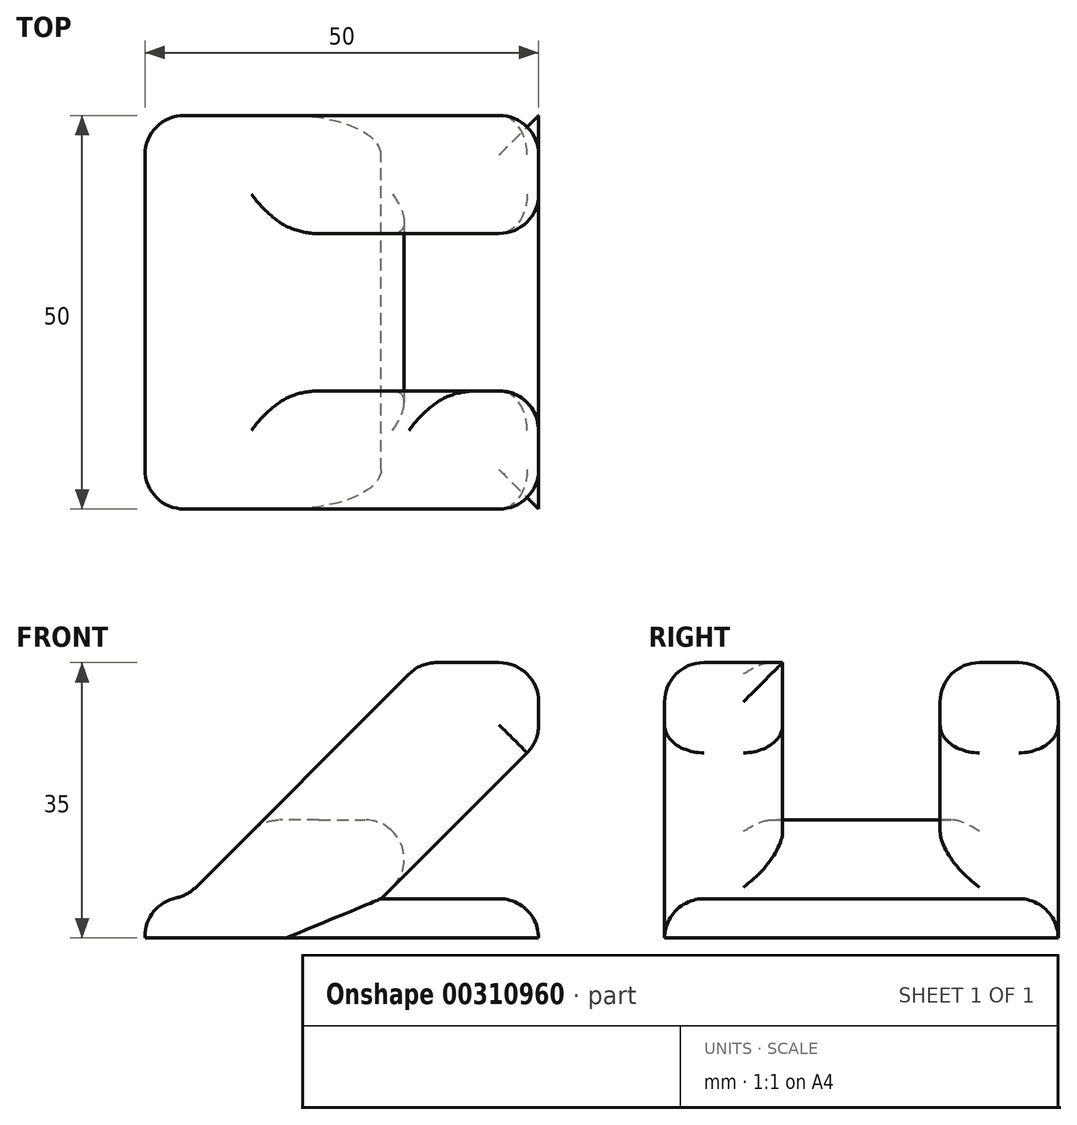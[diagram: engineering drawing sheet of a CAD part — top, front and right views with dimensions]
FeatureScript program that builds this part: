
annotation { "Feature Type Name" : "Feature", "Feature Type Description" : "" }
export const myFeature = defineFeature(function(context is Context, id is Id, definition is map)
    precondition{}
    {
        {
            var Q0;
            Q0=qCreatedBy(makeId("Front.planeOp"),FACE);
            var sketch = newSketch(context, id + "F0", { "sketchPlane" : qUnion([Q0])});
            skLineSegment(sketch, "E0", {"start": v(0, 0) * mm, "end": v(0, 5) * mm});
            skLineSegment(sketch, "E1", {"start": v(0, 5) * mm, "end": v(5, 5) * mm});
            skLineSegment(sketch, "E2", {"start": v(5, 5) * mm, "end": v(35, 35) * mm});
            skLineSegment(sketch, "E3", {"start": v(35, 35) * mm, "end": v(50, 35) * mm});
            skLineSegment(sketch, "E4", {"start": v(50, 35) * mm, "end": v(50, 25) * mm});
            skLineSegment(sketch, "E5", {"start": v(50, 25) * mm, "end": v(30, 5) * mm});
            skLineSegment(sketch, "E6", {"start": v(30, 5) * mm, "end": v(50, 5) * mm});
            skLineSegment(sketch, "E7", {"start": v(50, 5) * mm, "end": v(50, 0) * mm});
            skLineSegment(sketch, "E8", {"start": v(50, 0) * mm, "end": v(0, 0) * mm});
            skSolve(sketch);
        }
        {
            var Q0;
            Q0 = qSketchRegion(id + "F0", true);
            extrude(context, id + "F1", {"entities" : qUnion([Q0]), "depth" : 50 * mm});
        }
        {
            var Q0;
            Q0=makeQuery(id+"F1.opExtrude","SWEPT_FACE",FACE,{"disambiguationData":[OSD([sQuery(id+"F0.wireOp",EDGE,"E4")])]});
            var sketch = newSketch(context, id + "F2", { "sketchPlane" : qUnion([Q0])});
            skLineSegment(sketch, "E9.bottom", {"start": v(-35, 35) * mm, "end": v(-15, 35) * mm});
            skLineSegment(sketch, "E9.top", {"start": v(-35, 15) * mm, "end": v(-15, 15) * mm});
            skLineSegment(sketch, "E9.left", {"start": v(-35, 35) * mm, "end": v(-35, 15) * mm});
            skLineSegment(sketch, "E9.right", {"start": v(-15, 35) * mm, "end": v(-15, 15) * mm});
            skSolve(sketch);
        }
        {
            var Q0;
            Q0 = qSketchRegion(id + "F2", true);
            extrude(context, id + "F3", {"entities" : qUnion([Q0]), "operationType" : NewBodyOperationType.REMOVE, "endBound" : BoundingType.THROUGH_ALL, "oppositeDirection" : true, "depth" : 25 * mm});
        }
        {
            var Q0;
            Q0=makeQuery(id+"F1.opExtrude","CAP_EDGE",EDGE,{"disambiguationData":[OSD([sQuery(id+"F0.wireOp",EDGE,"E5")])],"isStart":false});
            var Q1;
            Q1=makeQuery(id+"F1.opExtrude","CAP_EDGE",EDGE,{"disambiguationData":[OSD([sQuery(id+"F0.wireOp",EDGE,"E4")])],"isStart":false});
            var Q2;
            Q2=makeQuery(id+"F3.boolean.opBoolean","COPY",EDGE,{"derivedFrom":makeQuery(id+"F3.opExtrude","CAP_EDGE",EDGE,{"disambiguationData":[OSD([sQuery(id+"F2.wireOp",EDGE,"E9.left")])],"isStart":true})});
            var Q3;
            Q3=makeQuery(id+"F3.boolean.opBoolean","INTERSECT",EDGE,{"derivedFrom":[makeQuery(id+"F1.opExtrude","SWEPT_FACE",FACE,{"disambiguationData":[OSD([sQuery(id+"F0.wireOp",EDGE,"E5")])]}),makeQuery(id+"F3.opExtrude","SWEPT_FACE",FACE,{"disambiguationData":[OSD([sQuery(id+"F2.wireOp",EDGE,"E9.left")])]})]});
            var Q4;
            Q4=makeQuery(id+"F3.boolean.opBoolean","INTERSECT",EDGE,{"derivedFrom":[makeQuery(id+"F1.opExtrude","SWEPT_FACE",FACE,{"disambiguationData":[OSD([sQuery(id+"F0.wireOp",EDGE,"E5")])]}),makeQuery(id+"F3.opExtrude","SWEPT_FACE",FACE,{"disambiguationData":[OSD([sQuery(id+"F2.wireOp",EDGE,"E9.top")])]})]});
            var Q5;
            Q5=makeQuery(id+"F3.boolean.opBoolean","INTERSECT",EDGE,{"derivedFrom":[makeQuery(id+"F1.opExtrude","SWEPT_FACE",FACE,{"disambiguationData":[OSD([sQuery(id+"F0.wireOp",EDGE,"E5")])]}),makeQuery(id+"F3.opExtrude","SWEPT_FACE",FACE,{"disambiguationData":[OSD([sQuery(id+"F2.wireOp",EDGE,"E9.right")])]})]});
            var Q6;
            Q6=makeQuery(id+"F3.boolean.opBoolean","COPY",EDGE,{"derivedFrom":makeQuery(id+"F3.opExtrude","CAP_EDGE",EDGE,{"disambiguationData":[OSD([sQuery(id+"F2.wireOp",EDGE,"E9.right")])],"isStart":true})});
            var Q7;
            Q7=makeQuery(id+"F1.opExtrude","CAP_EDGE",EDGE,{"disambiguationData":[OSD([sQuery(id+"F0.wireOp",EDGE,"E4")])],"isStart":true});
            var Q8;
            Q8=makeQuery(id+"F1.opExtrude","CAP_EDGE",EDGE,{"disambiguationData":[OSD([sQuery(id+"F0.wireOp",EDGE,"E5")])],"isStart":true});
            var Q9;
            {var subQ0=sQuery(id+"F0.wireOp",EDGE,"E3");var subQ1=sQuery(id+"F0.wireOp",EDGE,"E2");Q9=makeQuery(id+"F3.boolean.opBoolean","SPLIT",EDGE,{"disambiguationData":[TD([makeQuery(id+"F3.opExtrude","SWEPT_FACE",FACE,{"disambiguationData":[OSD([sQuery(id+"F2.wireOp",EDGE,"E9.right")])]})])],"derivedFrom":makeQuery(id+"F1.opExtrude","SWEPT_EDGE",EDGE,{"disambiguationData":[OSD([subQ1,subQ0])]})});}
            var Q10;
            {var subQ0=sQuery(id+"F0.wireOp",EDGE,"E3");var subQ1=sQuery(id+"F0.wireOp",EDGE,"E2");Q10=makeQuery(id+"F3.boolean.opBoolean","SPLIT",EDGE,{"disambiguationData":[TD([makeQuery(id+"F3.opExtrude","SWEPT_FACE",FACE,{"disambiguationData":[OSD([sQuery(id+"F2.wireOp",EDGE,"E9.left")])]})])],"derivedFrom":makeQuery(id+"F1.opExtrude","SWEPT_EDGE",EDGE,{"disambiguationData":[OSD([subQ1,subQ0])]})});}
            var Q11;
            Q11=makeQuery(id+"F3.boolean.opBoolean","COPY",EDGE,{"derivedFrom":makeQuery(id+"F3.opExtrude","SWEPT_EDGE",EDGE,{"disambiguationData":[OSD([sQuery(id+"F0.wireOp",EDGE,"E3"),sQuery(id+"F0.wireOp",EDGE,"E4"),sQuery(id+"F2.wireOp",EDGE,"E9.bottom"),sQuery(id+"F2.wireOp",EDGE,"E9.right")])]})});
            var Q12;
            Q12=makeQuery(id+"F3.boolean.opBoolean","COPY",EDGE,{"derivedFrom":makeQuery(id+"F3.opExtrude","SWEPT_EDGE",EDGE,{"disambiguationData":[OSD([sQuery(id+"F0.wireOp",EDGE,"E3"),sQuery(id+"F0.wireOp",EDGE,"E4"),sQuery(id+"F2.wireOp",EDGE,"E9.bottom"),sQuery(id+"F2.wireOp",EDGE,"E9.left")])]})});
            var Q13;
            Q13=makeQuery(id+"F1.opExtrude","CAP_EDGE",EDGE,{"disambiguationData":[OSD([sQuery(id+"F0.wireOp",EDGE,"E3")])],"isStart":false});
            var Q14;
            Q14=makeQuery(id+"F1.opExtrude","CAP_EDGE",EDGE,{"disambiguationData":[OSD([sQuery(id+"F0.wireOp",EDGE,"E3")])],"isStart":true});
            var Q15;
            Q15=makeQuery(id+"F1.opExtrude","CAP_EDGE",EDGE,{"disambiguationData":[OSD([sQuery(id+"F0.wireOp",EDGE,"E2")])],"isStart":true});
            var Q16;
            Q16=makeQuery(id+"F1.opExtrude","CAP_EDGE",EDGE,{"disambiguationData":[OSD([sQuery(id+"F0.wireOp",EDGE,"E2")])],"isStart":false});
            var Q17;
            Q17=makeQuery(id+"F3.boolean.opBoolean","INTERSECT",EDGE,{"derivedFrom":[makeQuery(id+"F1.opExtrude","SWEPT_FACE",FACE,{"disambiguationData":[OSD([sQuery(id+"F0.wireOp",EDGE,"E2")])]}),makeQuery(id+"F3.opExtrude","SWEPT_FACE",FACE,{"disambiguationData":[OSD([sQuery(id+"F2.wireOp",EDGE,"E9.right")])]})]});
            var Q18;
            Q18=makeQuery(id+"F3.boolean.opBoolean","INTERSECT",EDGE,{"derivedFrom":[makeQuery(id+"F1.opExtrude","SWEPT_FACE",FACE,{"disambiguationData":[OSD([sQuery(id+"F0.wireOp",EDGE,"E2")])]}),makeQuery(id+"F3.opExtrude","SWEPT_FACE",FACE,{"disambiguationData":[OSD([sQuery(id+"F2.wireOp",EDGE,"E9.left")])]})]});
            var Q19;
            Q19=makeQuery(id+"F3.boolean.opBoolean","INTERSECT",EDGE,{"derivedFrom":[makeQuery(id+"F1.opExtrude","SWEPT_FACE",FACE,{"disambiguationData":[OSD([sQuery(id+"F0.wireOp",EDGE,"E2")])]}),makeQuery(id+"F3.opExtrude","SWEPT_FACE",FACE,{"disambiguationData":[OSD([sQuery(id+"F2.wireOp",EDGE,"E9.top")])]})]});
            var Q20;
            Q20=makeQuery(id+"F1.opExtrude","SWEPT_EDGE",EDGE,{"disambiguationData":[OSD([sQuery(id+"F0.wireOp",EDGE,"E6"),sQuery(id+"F0.wireOp",EDGE,"E7")])]});
            var Q21;
            Q21=makeQuery(id+"F1.opExtrude","CAP_EDGE",EDGE,{"disambiguationData":[OSD([sQuery(id+"F0.wireOp",EDGE,"E6")])],"isStart":true});
            var Q22;
            Q22=makeQuery(id+"F1.opExtrude","CAP_EDGE",EDGE,{"disambiguationData":[OSD([sQuery(id+"F0.wireOp",EDGE,"E1")])],"isStart":true});
            var Q23;
            Q23=makeQuery(id+"F1.opExtrude","CAP_EDGE",EDGE,{"disambiguationData":[OSD([sQuery(id+"F0.wireOp",EDGE,"E1")])],"isStart":false});
            var Q24;
            Q24=makeQuery(id+"F1.opExtrude","CAP_EDGE",EDGE,{"disambiguationData":[OSD([sQuery(id+"F0.wireOp",EDGE,"E6")])],"isStart":false});
            var Q25;
            Q25=makeQuery(id+"F1.opExtrude","SWEPT_FACE",FACE,{"disambiguationData":[OSD([sQuery(id+"F0.wireOp",EDGE,"E2")])]});
            fillet(context, id + "F4", {"entities" : qUnion([Q0, Q1, Q2, Q3, Q4, Q5, Q6, Q7, Q8, Q9, Q10, Q11, Q12, Q13, Q14, Q15, Q16, Q17, Q18, Q19, Q20, Q21, Q22, Q23, Q24, Q25]), "radius" : 5 * mm, "tangentPropagation" : true, "allowEdgeOverflow" : false});
        }
        {
            var Q0;
            {var subQ0=sQuery(id+"F0.wireOp",EDGE,"E5");var subQ1=sQuery(id+"F0.wireOp",EDGE,"E4");Q0=makeQuery(id+"F3.boolean.opBoolean","SPLIT",EDGE,{"disambiguationData":[TD([makeQuery(id+"F3.opExtrude","SWEPT_FACE",FACE,{"disambiguationData":[OSD([sQuery(id+"F2.wireOp",EDGE,"E9.right")])]})])],"derivedFrom":makeQuery(id+"F1.opExtrude","SWEPT_EDGE",EDGE,{"disambiguationData":[OSD([subQ1,subQ0])]})});}
            var Q1;
            {var subQ0=sQuery(id+"F0.wireOp",EDGE,"E4");var subQ1=sQuery(id+"F0.wireOp",EDGE,"E3");Q1=makeQuery(id+"F3.boolean.opBoolean","SPLIT",EDGE,{"disambiguationData":[TD([makeQuery(id+"F3.opExtrude","SWEPT_FACE",FACE,{"disambiguationData":[OSD([sQuery(id+"F2.wireOp",EDGE,"E9.right")])]})])],"derivedFrom":makeQuery(id+"F1.opExtrude","SWEPT_EDGE",EDGE,{"disambiguationData":[OSD([subQ1,subQ0])]})});}
            var Q2;
            {var subQ0=sQuery(id+"F0.wireOp",EDGE,"E4");var subQ1=sQuery(id+"F0.wireOp",EDGE,"E3");Q2=makeQuery(id+"F3.boolean.opBoolean","SPLIT",EDGE,{"disambiguationData":[TD([makeQuery(id+"F3.opExtrude","SWEPT_FACE",FACE,{"disambiguationData":[OSD([sQuery(id+"F2.wireOp",EDGE,"E9.left")])]})])],"derivedFrom":makeQuery(id+"F1.opExtrude","SWEPT_EDGE",EDGE,{"disambiguationData":[OSD([subQ1,subQ0])]})});}
            var Q3;
            {var subQ0=sQuery(id+"F0.wireOp",EDGE,"E5");var subQ1=sQuery(id+"F0.wireOp",EDGE,"E4");Q3=makeQuery(id+"F3.boolean.opBoolean","SPLIT",EDGE,{"disambiguationData":[TD([makeQuery(id+"F3.opExtrude","SWEPT_FACE",FACE,{"disambiguationData":[OSD([sQuery(id+"F2.wireOp",EDGE,"E9.left")])]})])],"derivedFrom":makeQuery(id+"F1.opExtrude","SWEPT_EDGE",EDGE,{"disambiguationData":[OSD([subQ1,subQ0])]})});}
            var Q4;
            Q4=makeQuery(id+"F1.opExtrude","SWEPT_EDGE",EDGE,{"disambiguationData":[OSD([sQuery(id+"F0.wireOp",EDGE,"E0"),sQuery(id+"F0.wireOp",EDGE,"E1")])]});
            fillet(context, id + "F5", {"entities" : qUnion([Q0, Q1, Q2, Q3, Q4]), "radius" : 5 * mm, "tangentPropagation" : true, "allowEdgeOverflow" : false});
        }
    });
